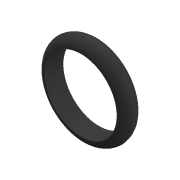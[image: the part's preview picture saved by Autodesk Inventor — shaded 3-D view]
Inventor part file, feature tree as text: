
AUTODESK INVENTOR PART (.ipt)
format: ipt  version: 2020 (Build 240168000, 168)  size: 125,952 bytes
history: native  units: mm
features: other x1, extrude x1, fillet x1, sketch x1
ambient origin geometry x8: Origin, YZ Plane, XZ Plane, XY Plane, X Axis, Y Axis, Z Axis, Center Point
bodies: Body1 (feature_tree)
feature tree (4):
  other  "솔리드1"
  extrude  "돌출1"  Depth=120.0mm
  fillet  "모깎기1"  Radius=150.0mm
  sketch  "스케치1"
